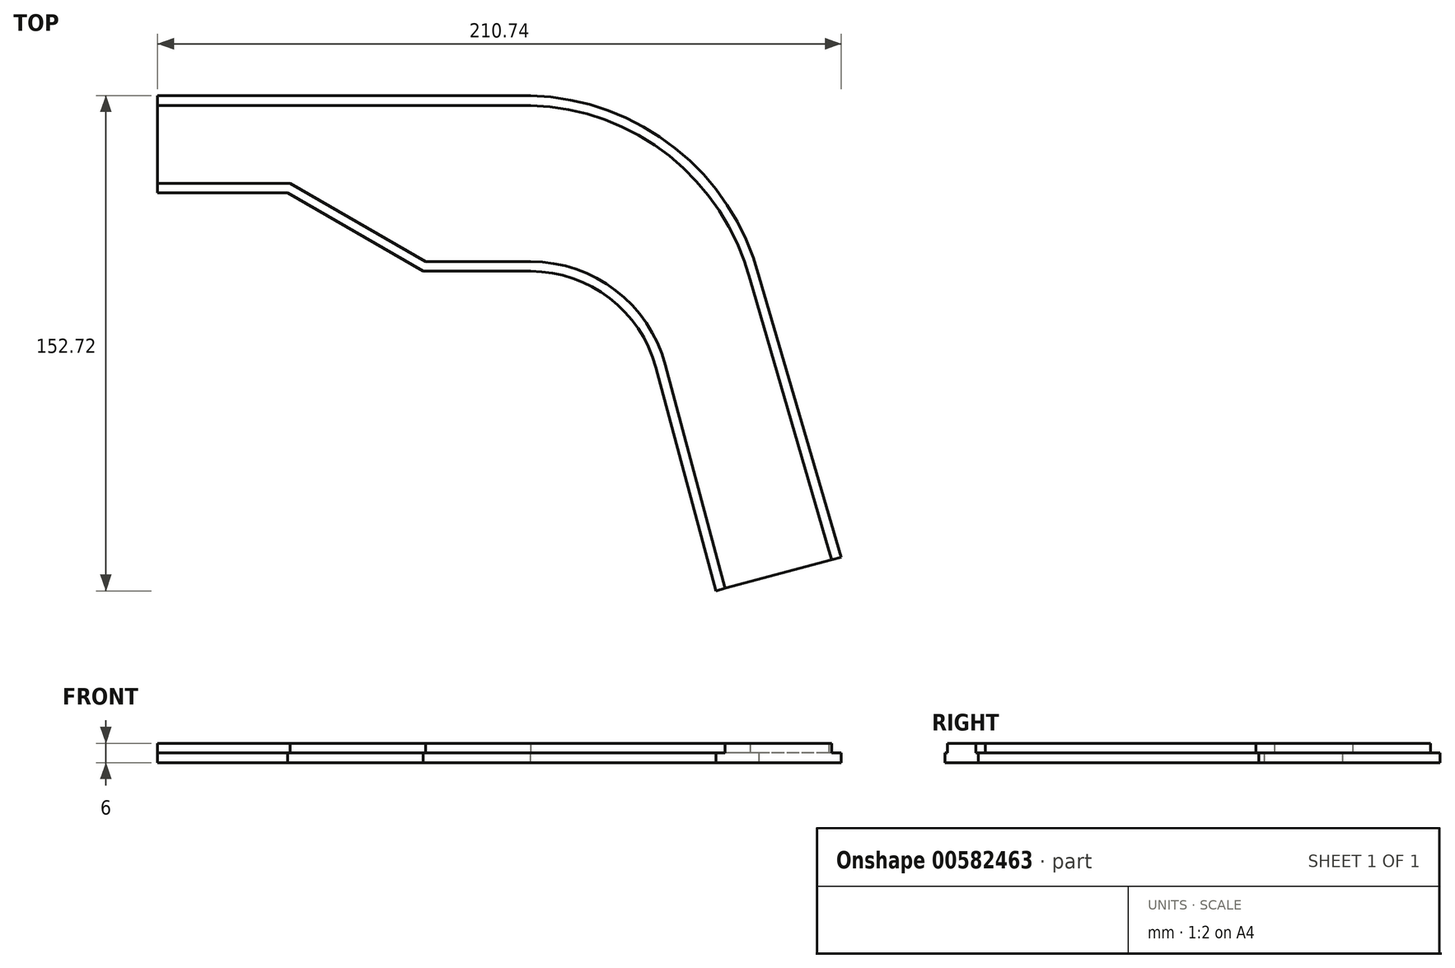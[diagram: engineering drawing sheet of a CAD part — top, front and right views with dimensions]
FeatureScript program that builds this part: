
annotation { "Feature Type Name" : "Feature", "Feature Type Description" : "" }
export const myFeature = defineFeature(function(context is Context, id is Id, definition is map)
    precondition{}
    {
        {
            var Q0;
            Q0=qCreatedBy(makeId("Top.planeOp"),FACE);
            var sketch = newSketch(context, id + "F0", { "sketchPlane" : qUnion([Q0])});
            skLineSegment(sketch, "E0", {"start": v(0, 0) * mm, "end": v(-115, 0) * mm});
            skLineSegment(sketch, "E1", {"start": v(-115, 0) * mm, "end": v(-115, -30) * mm});
            skLineSegment(sketch, "E2", {"start": v(-115, -30) * mm, "end": v(-75, -30) * mm});
            skPoint(sketch, "E3.end.orphan", {"position": v(0, -54.16) * mm});
            skLineSegment(sketch, "E4", {"start": v(-75, -30) * mm, "end": v(-33.15, -54.16) * mm});
            skLineSegment(sketch, "E5", {"start": v(-33.15, -54.16) * mm, "end": v(0, -54.16) * mm});
            skArc(sketch, "E6", {"start": v(38.64, -83.8) * mm, "mid": v(24.35, -62.43) * mm, "end": v(0, -54.16) * mm});
            skArc(sketch, "E7", {"start": v(70.52, -55.97) * mm, "mid": v(44.6, -16.23) * mm, "end": v(0, 0) * mm});
            skPoint(sketch, "E8", {"position": v(0, -149.94) * mm});
            skPoint(sketch, "E9", {"position": v(0, -134.16) * mm});
            skLineSegment(sketch, "E10", {"start": v(38.64, -83.8) * mm, "end": v(57.1, -152.72) * mm});
            skLineSegment(sketch, "E11", {"start": v(57.1, -152.72) * mm, "end": v(95.74, -142.37) * mm});
            skLineSegment(sketch, "E12", {"start": v(95.74, -142.37) * mm, "end": v(70.52, -55.97) * mm});
            skSolve(sketch);
        }
        {
            var Q0;
            Q0 = qSketchRegion(id + "F0", true);
            extrude(context, id + "F1", {"entities" : qUnion([Q0]), "oppositeDirection" : true, "depth" : 3 * mm, "offsetDistance" : 25 * mm});
        }
        {
            var Q0;
            Q0=makeQuery(id+"F1.opExtrude","CAP_FACE",FACE,{"disambiguationData":[OSD([sQuery(id+"F0.wireOp",EDGE,"E0"),sQuery(id+"F0.wireOp",EDGE,"E1"),sQuery(id+"F0.wireOp",EDGE,"E2"),sQuery(id+"F0.wireOp",EDGE,"E4"),sQuery(id+"F0.wireOp",EDGE,"E5"),sQuery(id+"F0.wireOp",EDGE,"E6"),sQuery(id+"F0.wireOp",EDGE,"E7"),sQuery(id+"F0.wireOp",EDGE,"E10"),sQuery(id+"F0.wireOp",EDGE,"E11"),sQuery(id+"F0.wireOp",EDGE,"E12")])],"isStart":true});
            var sketch = newSketch(context, id + "F2", { "sketchPlane" : qUnion([Q0])});
            skLineSegment(sketch, "E13.0", {"start": v(41.53, -83.03) * mm, "end": v(59.22, -149.04) * mm});
            skArc(sketch, "E13.1", {"start": v(0, -51.16) * mm, "mid": v(26.18, -60.05) * mm, "end": v(41.53, -83.03) * mm});
            skLineSegment(sketch, "E13.2", {"start": v(59.22, -149.04) * mm, "end": v(92, -140.26) * mm});
            skLineSegment(sketch, "E13.3", {"start": v(-32.35, -51.16) * mm, "end": v(0, -51.16) * mm});
            skLineSegment(sketch, "E13.4", {"start": v(-74.2, -27) * mm, "end": v(-32.35, -51.16) * mm});
            skLineSegment(sketch, "E13.5", {"start": v(-112, -27) * mm, "end": v(-74.2, -27) * mm});
            skLineSegment(sketch, "E13.6", {"start": v(92, -140.26) * mm, "end": v(67.63, -56.77) * mm});
            skArc(sketch, "E13.7", {"start": v(67.63, -56.77) * mm, "mid": v(42.76, -18.6) * mm, "end": v(-0.04, -3) * mm});
            skLineSegment(sketch, "E13.8", {"start": v(-0.04, -3) * mm, "end": v(-112, -3) * mm});
            skLineSegment(sketch, "E13.9", {"start": v(-112, -3) * mm, "end": v(-112, -27) * mm});
            skSolve(sketch);
        }
        {
            var Q0;
            Q0 = qSketchRegion(id + "F2", true);
            extrude(context, id + "F3", {"entities" : qUnion([Q0]), "operationType" : NewBodyOperationType.ADD, "depth" : 3 * mm, "offsetDistance" : 25 * mm});
        }
        {
            var Q0;
            Q0=makeQuery(id+"F3.opExtrude","SWEPT_FACE",FACE,{"disambiguationData":[OSD([sQuery(id+"F2.wireOp",EDGE,"E13.9")])]});
            var sketch = newSketch(context, id + "F4", { "sketchPlane" : qUnion([Q0])});
            skLineSegment(sketch, "E14.bottom", {"start": v(3, 3) * mm, "end": v(27, 3) * mm});
            skLineSegment(sketch, "E14.top", {"start": v(3, 0) * mm, "end": v(27, 0) * mm});
            skLineSegment(sketch, "E14.left", {"start": v(3, 3) * mm, "end": v(3, 0) * mm});
            skLineSegment(sketch, "E14.right", {"start": v(27, 3) * mm, "end": v(27, 0) * mm});
            skSolve(sketch);
        }
        {
            var Q0;
            Q0 = qSketchRegion(id + "F4", true);
            extrude(context, id + "F5", {"entities" : qUnion([Q0]), "operationType" : NewBodyOperationType.ADD, "depth" : 3 * mm, "offsetDistance" : 25 * mm});
        }
        {
            var Q0;
            Q0=makeQuery(id+"F3.opExtrude","SWEPT_FACE",FACE,{"disambiguationData":[OSD([sQuery(id+"F2.wireOp",EDGE,"E13.2")])]});
            var sketch = newSketch(context, id + "F6", { "sketchPlane" : qUnion([Q0])});
            skLineSegment(sketch, "E15.bottom", {"start": v(18.63, 3) * mm, "end": v(52.56, 3) * mm});
            skLineSegment(sketch, "E15.top", {"start": v(18.63, 0) * mm, "end": v(52.56, 0) * mm});
            skLineSegment(sketch, "E15.left", {"start": v(18.63, 3) * mm, "end": v(18.63, 0) * mm});
            skLineSegment(sketch, "E15.right", {"start": v(52.56, 3) * mm, "end": v(52.56, 0) * mm});
            skSolve(sketch);
        }
        {
            var Q0;
            Q0 = qSketchRegion(id + "F6", true);
            extrude(context, id + "F7", {"entities" : qUnion([Q0]), "operationType" : NewBodyOperationType.ADD, "depth" : 3 * mm, "offsetDistance" : 25 * mm});
        }
    });
